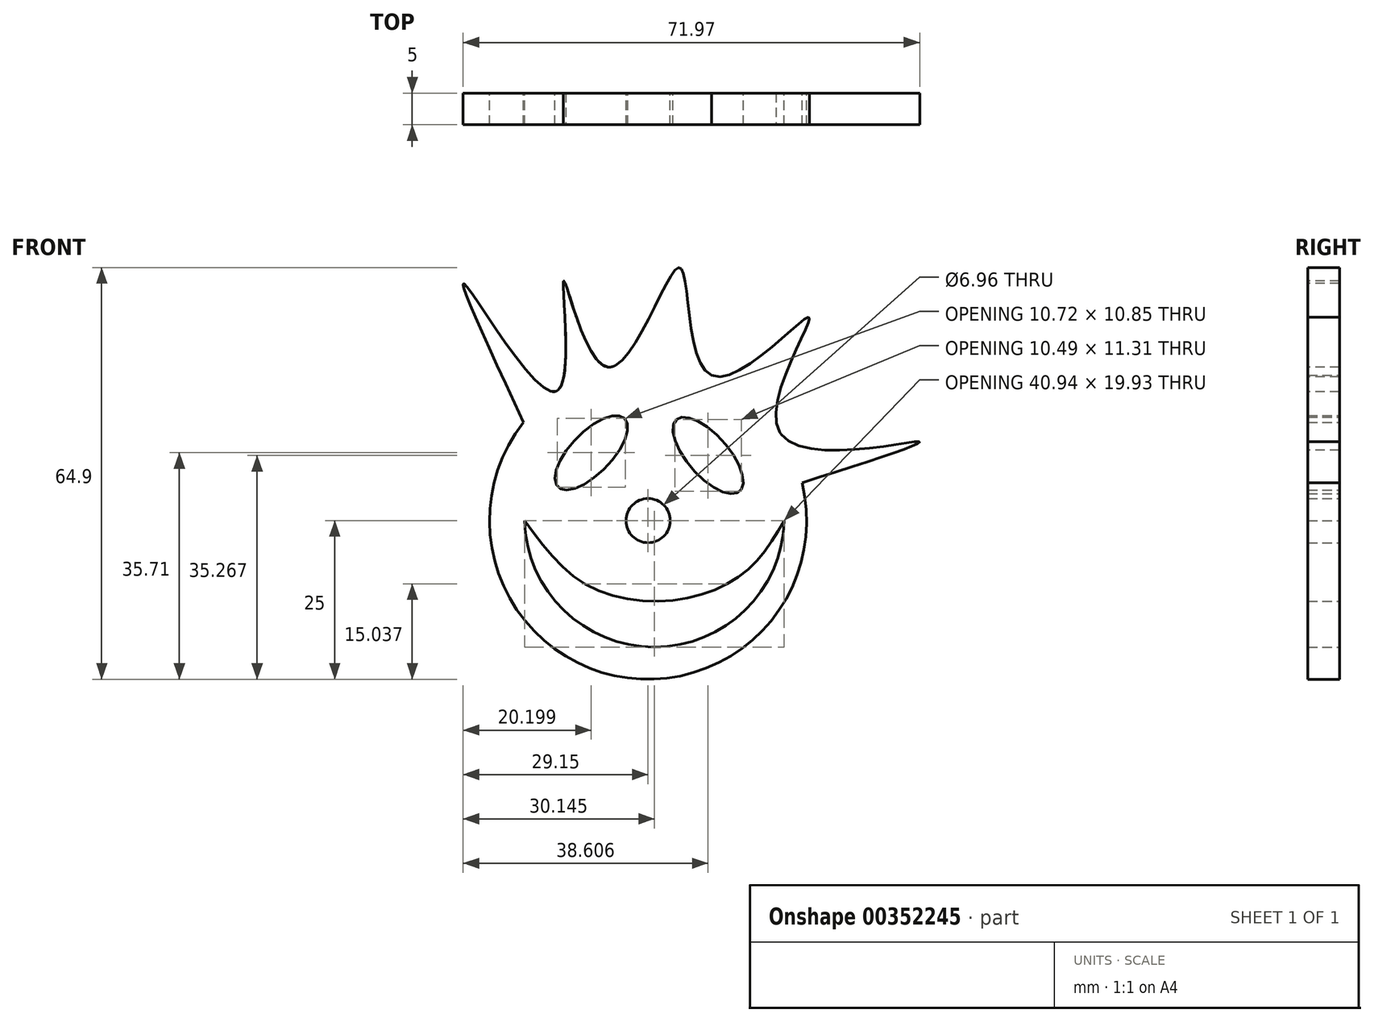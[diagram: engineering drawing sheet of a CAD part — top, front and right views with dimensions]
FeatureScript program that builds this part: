
annotation { "Feature Type Name" : "Feature", "Feature Type Description" : "" }
export const myFeature = defineFeature(function(context is Context, id is Id, definition is map)
    precondition{}
    {
        {
            var Q0;
            Q0=qCreatedBy(makeId("Front.planeOp"),FACE);
            var sketch = newSketch(context, id + "F0", { "sketchPlane" : qUnion([Q0])});
            skArc(sketch, "E0", {"start": v(-19.63, 15.48) * mm, "mid": v(-5.3, -24.43) * mm, "end": v(24.28, 5.97) * mm});
            skArc(sketch, "E1", {"start": v(-19.48, 0) * mm, "mid": v(1, -19.93) * mm, "end": v(21.47, 0) * mm});
            skFitSpline(sketch, "E2", {"points": [v(-19.48, 0) * mm, v(-9.63, -10.16) * mm, v(4.6, -12.46) * mm, v(15.7, -7.75) * mm, v(21.47, 0) * mm], "startDerivative": vector(32.51, -44.35) * mm, "endDerivative": vector(22.17, 38.02) * mm});
            skCircle(sketch, "E3", {"center": v(0, 0) * mm, "radius": 3.48 * mm});
            skFitSpline(sketch, "E4", {"points": [v(-19.63, 15.48) * mm, v(-28.7, 37.07) * mm, v(-14.36, 20.47) * mm, v(-13.3, 37.8) * mm, v(-6.26, 24.2) * mm, v(4.92, 39.9) * mm, v(10.04, 22.9) * mm, v(25.34, 32.04) * mm, v(20.75, 13.94) * mm, v(42.52, 12.46) * mm, v(24.28, 5.97) * mm], "startDerivative": vector(-151.91, 326.99) * mm, "endDerivative": vector(-305.53, -97.9) * mm});
            skArc(sketch, "E5.trimOffspring", {"start": v(-14.2, 20.57) * mm, "mid": v(-14.28, 20.52) * mm, "end": v(-14.36, 20.47) * mm});
            skArc(sketch, "E6.trimOffspring", {"start": v(-5.17, 24.46) * mm, "mid": v(-5.72, 24.34) * mm, "end": v(-6.26, 24.2) * mm});
            skArc(sketch, "E7.trimOffspring", {"start": v(10.04, 22.9) * mm, "mid": v(10, 22.9) * mm, "end": v(9.98, 22.92) * mm});
            skArc(sketch, "E8.trimOffspring", {"start": v(20.98, 13.6) * mm, "mid": v(20.86, 13.77) * mm, "end": v(20.75, 13.94) * mm});
            skSolve(sketch);
        }
        {
            var Q0;
            Q0=makeQuery(id+"F0.imprint","IMPRINT",FACE,{"disambiguationData":[TD([[makeQuery(id+"F0.imprint","IMPRINT",EDGE,{"derivedFrom":sQuery(id+"F0.wireOp",EDGE,"E0")}),1.0]])]});
            extrude(context, id + "F1", {"entities" : qUnion([Q0]), "depth" : 5 * mm});
        }
        {
            var Q0;
            Q0=makeQuery(id+"F1.opExtrude","CAP_FACE",FACE,{"disambiguationData":[OSD([sQuery(id+"F0.wireOp",EDGE,"E0"),sQuery(id+"F0.wireOp",EDGE,"E1"),sQuery(id+"F0.wireOp",EDGE,"E2"),sQuery(id+"F0.wireOp",EDGE,"E3"),sQuery(id+"F0.wireOp",EDGE,"E4"),sQuery(id+"F0.wireOp",EDGE,"E7.trimOffspring")])],"isStart":false});
            var sketch = newSketch(context, id + "F2", { "sketchPlane" : qUnion([Q0])});
            skEllipse(sketch, "E9", {"center": v(-8.95, 10.7) * mm, "majorRadius": 7.54 * mm, "minorRadius": 3.25 * mm, "majorAxis": v(0.7, 0.72)});
            skLineSegment(sketch, "E10", {"start": v(0, 0) * mm, "end": v(0.97, 40.13) * mm, "construction": true});
            skEllipse(sketch, "E11.MirrorC", {"center": v(9.46, 10.27) * mm, "majorRadius": 7.54 * mm, "minorRadius": 3.25 * mm, "majorAxis": v(-0.66, 0.75)});
            skSolve(sketch);
        }
        {
            var Q0;
            Q0 = qSketchRegion(id + "F2", true);
            extrude(context, id + "F3", {"entities" : qUnion([Q0]), "operationType" : NewBodyOperationType.REMOVE, "oppositeDirection" : true, "depth" : 10 * mm, "offsetDistance" : 25 * mm});
        }
    });
